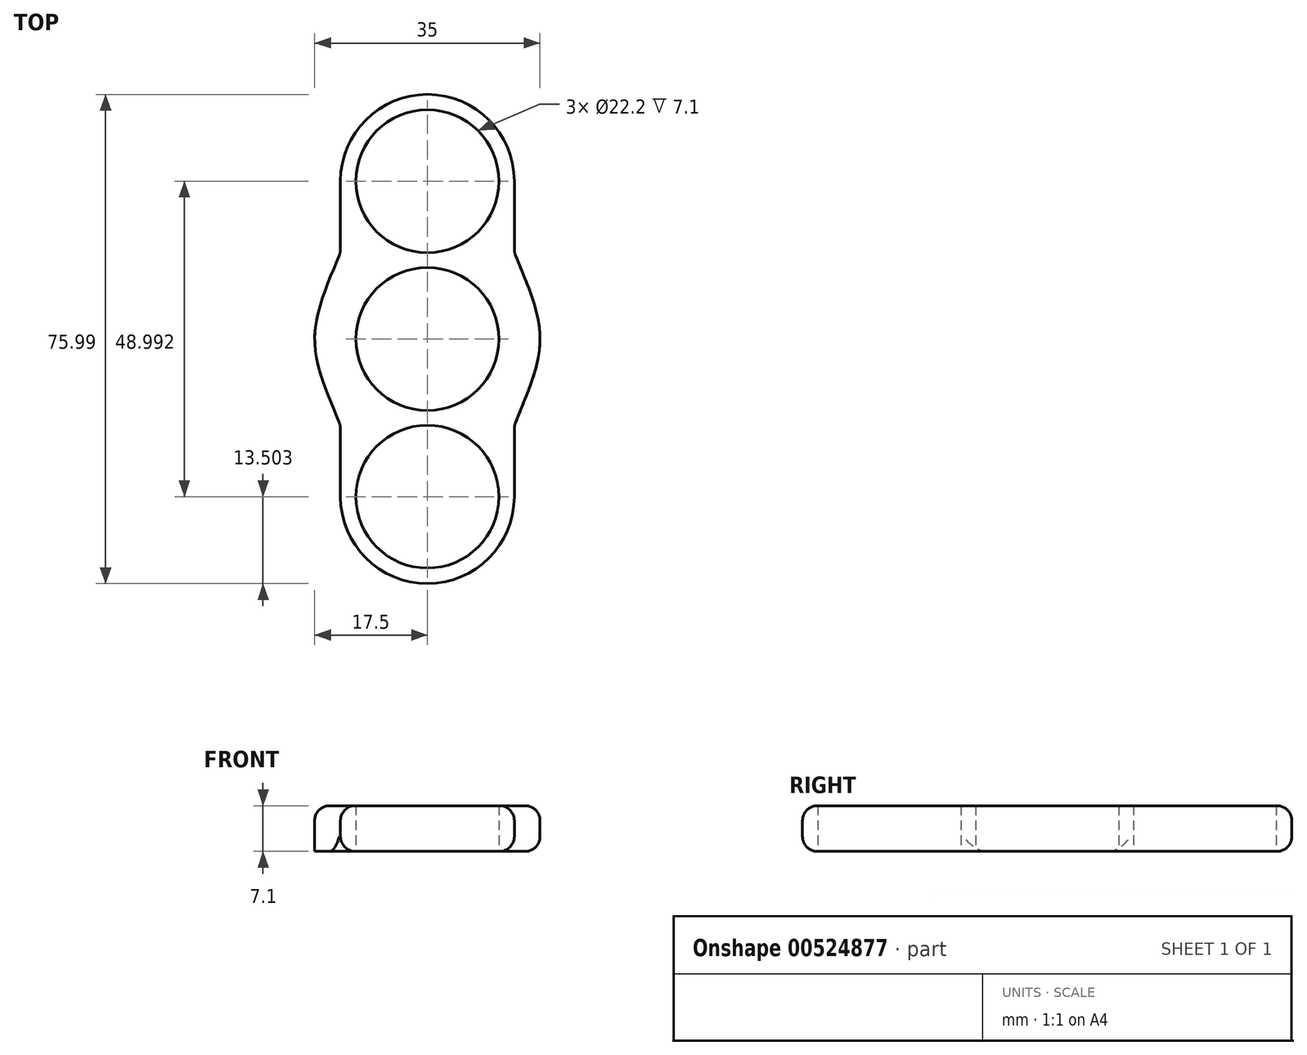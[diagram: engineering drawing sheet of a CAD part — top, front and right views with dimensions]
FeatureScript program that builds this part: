
annotation { "Feature Type Name" : "Feature", "Feature Type Description" : "" }
export const myFeature = defineFeature(function(context is Context, id is Id, definition is map)
    precondition{}
    {
        {
            var Q0;
            Q0=qCreatedBy(makeId("Top.planeOp"),FACE);
            var sketch = newSketch(context, id + "F0", { "sketchPlane" : qUnion([Q0])});
            skCircle(sketch, "E0", {"center": v(0, 0) * mm, "radius": 11.1 * mm});
            skCircle(sketch, "E1.cCircle", {"center": v(0, 0) * mm, "radius": 13.5 * mm, "construction": true});
            skLineSegment(sketch, "E1.0", {"start": v(13.5, 13.5) * mm, "end": v(13.5, -13.5) * mm});
            skLineSegment(sketch, "E1.1", {"start": v(13.5, -13.5) * mm, "end": v(-13.5, -13.5) * mm});
            skLineSegment(sketch, "E1.2", {"start": v(-13.5, -13.5) * mm, "end": v(-13.5, 13.5) * mm});
            skLineSegment(sketch, "E1.3", {"start": v(-13.5, 13.5) * mm, "end": v(13.5, 13.5) * mm});
            skPoint(sketch, "E1.0.midPoint", {"position": v(13.5, 0) * mm});
            skCircle(sketch, "E2", {"center": v(0, 24.5) * mm, "radius": 11.1 * mm});
            skPoint(sketch, "E2.centerSnap0", {"position": v(0, 13.5) * mm});
            skCircle(sketch, "E3", {"center": v(0, -24.5) * mm, "radius": 11.1 * mm});
            skLineSegment(sketch, "E4.top", {"start": v(-13.5, 24.5) * mm, "end": v(13.5, 24.5) * mm});
            skLineSegment(sketch, "E4.left", {"start": v(-13.5, 13.5) * mm, "end": v(-13.5, 24.5) * mm});
            skLineSegment(sketch, "E4.right", {"start": v(13.5, 13.5) * mm, "end": v(13.5, 24.5) * mm});
            skLineSegment(sketch, "E5.bottom", {"start": v(-13.5, -13.5) * mm, "end": v(13.5, -13.5) * mm});
            skLineSegment(sketch, "E5.top", {"start": v(-13.5, -24.5) * mm, "end": v(13.5, -24.5) * mm});
            skLineSegment(sketch, "E5.left", {"start": v(-13.5, -13.5) * mm, "end": v(-13.5, -24.5) * mm});
            skLineSegment(sketch, "E5.right", {"start": v(13.5, -13.5) * mm, "end": v(13.5, -24.5) * mm});
            skArc(sketch, "E6", {"start": v(-13.5, -24.5) * mm, "mid": v(0, -38) * mm, "end": v(13.5, -24.5) * mm});
            skArc(sketch, "E7", {"start": v(13.5, 24.5) * mm, "mid": v(0, 38) * mm, "end": v(-13.5, 24.5) * mm});
            skFitSpline(sketch, "E8", {"points": [v(13.5, 13.5) * mm, v(17.5, 0) * mm, v(13.5, -13.5) * mm], "startDerivative": vector(10.46, -27) * mm, "endDerivative": vector(-10.46, -27) * mm});
            skFitSpline(sketch, "E9", {"points": [v(-13.5, 13.5) * mm, v(-17.5, 0) * mm, v(-13.5, -13.5) * mm], "startDerivative": vector(-10.46, -27) * mm, "endDerivative": vector(10.46, -27) * mm});
            skSolve(sketch);
        }
        {
            var Q0;
            {var subQ4=sQuery(id+"F0.wireOp",EDGE,"E7");Q0=makeQuery(id+"F0.imprint","IMPRINT",FACE,{"disambiguationData":[TD([[makeQuery(id+"F0.imprint","IMPRINT",EDGE,{"derivedFrom":subQ4}),1.0]])]});}
            var Q1;
            {var subQ5=sQuery(id+"F0.wireOp",EDGE,"E4.left");Q1=makeQuery(id+"F0.imprint","IMPRINT",FACE,{"disambiguationData":[TD([[makeQuery(id+"F0.imprint","IMPRINT",EDGE,{"derivedFrom":subQ5}),-1.0]])]});}
            var Q2;
            {var subQ5=sQuery(id+"F0.wireOp",EDGE,"E4.right");Q2=makeQuery(id+"F0.imprint","IMPRINT",FACE,{"disambiguationData":[TD([[makeQuery(id+"F0.imprint","IMPRINT",EDGE,{"derivedFrom":subQ5}),1.0]])]});}
            var Q3;
            Q3=makeQuery(id+"F0.imprint","IMPRINT",FACE,{"disambiguationData":[TD([[makeQuery(id+"F0.imprint","IMPRINT",EDGE,{"derivedFrom":sQuery(id+"F0.wireOp",EDGE,"E0")}),-1.0]])]});
            var Q4;
            Q4=makeQuery(id+"F0.imprint","IMPRINT",FACE,{"disambiguationData":[TD([[makeQuery(id+"F0.imprint","IMPRINT",EDGE,{"derivedFrom":sQuery(id+"F0.wireOp",EDGE,"E1.0")}),1.0]])]});
            var Q5;
            Q5=makeQuery(id+"F0.imprint","IMPRINT",FACE,{"disambiguationData":[TD([[makeQuery(id+"F0.imprint","IMPRINT",EDGE,{"derivedFrom":sQuery(id+"F0.wireOp",EDGE,"E1.2")}),1.0]])]});
            var Q6;
            {var subQ5=sQuery(id+"F0.wireOp",EDGE,"E5.left");Q6=makeQuery(id+"F0.imprint","IMPRINT",FACE,{"disambiguationData":[TD([[makeQuery(id+"F0.imprint","IMPRINT",EDGE,{"derivedFrom":subQ5}),1.0]])]});}
            var Q7;
            {var subQ5=sQuery(id+"F0.wireOp",EDGE,"E5.right");Q7=makeQuery(id+"F0.imprint","IMPRINT",FACE,{"disambiguationData":[TD([[makeQuery(id+"F0.imprint","IMPRINT",EDGE,{"derivedFrom":subQ5}),-1.0]])]});}
            var Q8;
            {var subQ4=sQuery(id+"F0.wireOp",EDGE,"E6");Q8=makeQuery(id+"F0.imprint","IMPRINT",FACE,{"disambiguationData":[TD([[makeQuery(id+"F0.imprint","IMPRINT",EDGE,{"derivedFrom":subQ4}),1.0]])]});}
            extrude(context, id + "F1", {"entities" : qUnion([Q0, Q1, Q2, Q3, Q4, Q5, Q6, Q7, Q8]), "depth" : 7.1 * mm, "offsetDistance" : 25 * mm});
        }
        {
            var Q0;
            Q0=makeQuery(id+"F1.opExtrude","SWEPT_EDGE",EDGE,{"disambiguationData":[OSD([sQuery(id+"F0.wireOp",EDGE,"E1.0"),sQuery(id+"F0.wireOp",EDGE,"E5.bottom"),sQuery(id+"F0.wireOp",EDGE,"E5.right"),sQuery(id+"F0.wireOp",EDGE,"E8")])]});
            var Q1;
            Q1=makeQuery(id+"F1.opExtrude","CAP_EDGE",EDGE,{"disambiguationData":[OSD([sQuery(id+"F0.wireOp",EDGE,"E8")])],"isStart":false});
            var Q2;
            Q2=makeQuery(id+"F1.opExtrude","CAP_EDGE",EDGE,{"disambiguationData":[OSD([sQuery(id+"F0.wireOp",EDGE,"E8")])],"isStart":true});
            var Q3;
            Q3=makeQuery(id+"F1.opExtrude","SWEPT_EDGE",EDGE,{"disambiguationData":[OSD([sQuery(id+"F0.wireOp",EDGE,"E1.0"),sQuery(id+"F0.wireOp",EDGE,"E1.3"),sQuery(id+"F0.wireOp",EDGE,"E4.right"),sQuery(id+"F0.wireOp",EDGE,"E8")])]});
            var Q4;
            Q4=makeQuery(id+"F1.opExtrude","CAP_EDGE",EDGE,{"disambiguationData":[OSD([sQuery(id+"F0.wireOp",EDGE,"E4.right")])],"isStart":false});
            var Q5;
            Q5=makeQuery(id+"F1.opExtrude","CAP_EDGE",EDGE,{"disambiguationData":[OSD([sQuery(id+"F0.wireOp",EDGE,"E7")])],"isStart":false});
            var Q6;
            Q6=makeQuery(id+"F1.opExtrude","CAP_EDGE",EDGE,{"disambiguationData":[OSD([sQuery(id+"F0.wireOp",EDGE,"E7")])],"isStart":true});
            var Q7;
            Q7=makeQuery(id+"F1.opExtrude","SWEPT_FACE",FACE,{"disambiguationData":[OSD([sQuery(id+"F0.wireOp",EDGE,"E4.right")])]});
            var Q8;
            Q8=makeQuery(id+"F1.opExtrude","CAP_EDGE",EDGE,{"disambiguationData":[OSD([sQuery(id+"F0.wireOp",EDGE,"E4.left")])],"isStart":false});
            var Q9;
            Q9=makeQuery(id+"F1.opExtrude","CAP_EDGE",EDGE,{"disambiguationData":[OSD([sQuery(id+"F0.wireOp",EDGE,"E9")])],"isStart":false});
            var Q10;
            Q10=makeQuery(id+"F1.opExtrude","CAP_EDGE",EDGE,{"disambiguationData":[OSD([sQuery(id+"F0.wireOp",EDGE,"E6")])],"isStart":false});
            var Q11;
            Q11=makeQuery(id+"F1.opExtrude","CAP_EDGE",EDGE,{"disambiguationData":[OSD([sQuery(id+"F0.wireOp",EDGE,"E5.left")])],"isStart":false});
            var Q12;
            Q12=makeQuery(id+"F1.opExtrude","CAP_EDGE",EDGE,{"disambiguationData":[OSD([sQuery(id+"F0.wireOp",EDGE,"E5.right")])],"isStart":false});
            var Q13;
            Q13=makeQuery(id+"F1.opExtrude","CAP_EDGE",EDGE,{"disambiguationData":[OSD([sQuery(id+"F0.wireOp",EDGE,"E5.right")])],"isStart":true});
            var Q14;
            Q14=makeQuery(id+"F1.opExtrude","CAP_EDGE",EDGE,{"disambiguationData":[OSD([sQuery(id+"F0.wireOp",EDGE,"E6")])],"isStart":true});
            var Q15;
            Q15=makeQuery(id+"F1.opExtrude","SWEPT_EDGE",EDGE,{"disambiguationData":[OSD([sQuery(id+"F0.wireOp",EDGE,"E1.2"),sQuery(id+"F0.wireOp",EDGE,"E5.bottom"),sQuery(id+"F0.wireOp",EDGE,"E5.left"),sQuery(id+"F0.wireOp",EDGE,"E9")])]});
            var Q16;
            Q16=makeQuery(id+"F1.opExtrude","SWEPT_EDGE",EDGE,{"disambiguationData":[OSD([sQuery(id+"F0.wireOp",EDGE,"E1.2"),sQuery(id+"F0.wireOp",EDGE,"E1.3"),sQuery(id+"F0.wireOp",EDGE,"E4.left"),sQuery(id+"F0.wireOp",EDGE,"E9")])]});
            fillet(context, id + "F2", {"entities" : qUnion([Q0, Q1, Q2, Q3, Q4, Q5, Q6, Q7, Q8, Q9, Q10, Q11, Q12, Q13, Q14, Q15, Q16]), "radius" : 2.3 * mm, "tangentPropagation" : true, "allowEdgeOverflow" : false});
        }
    });
